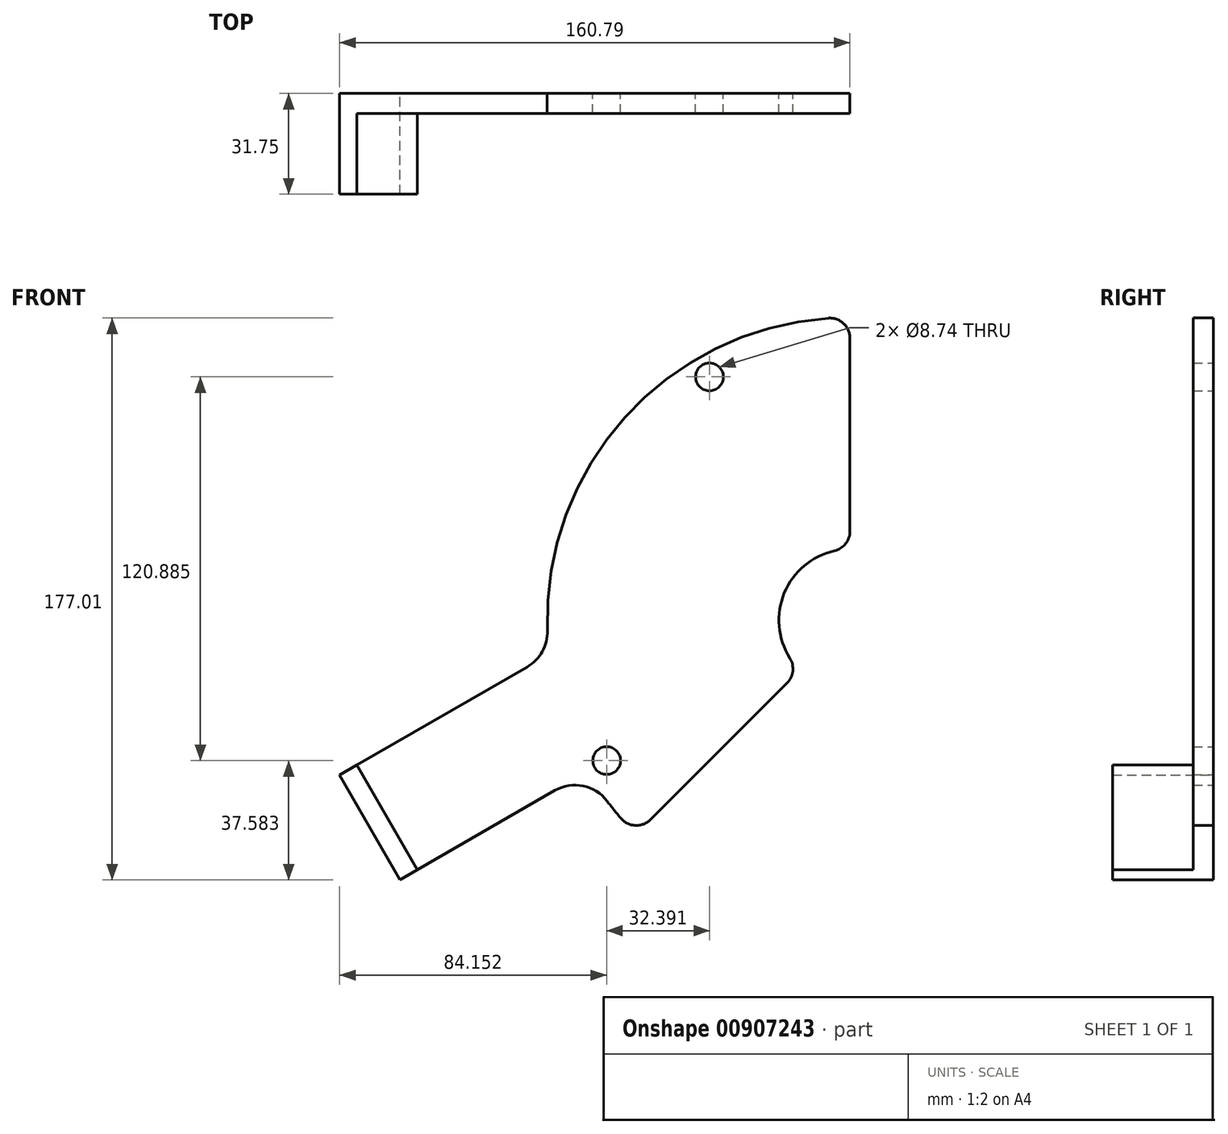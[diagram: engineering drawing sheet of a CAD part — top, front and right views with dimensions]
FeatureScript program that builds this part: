
annotation { "Feature Type Name" : "Feature", "Feature Type Description" : "" }
export const myFeature = defineFeature(function(context is Context, id is Id, definition is map)
    precondition{}
    {
        {
            var Q0;
            Q0=qCreatedBy(makeId("Front.planeOp"),FACE);
            var sketch = newSketch(context, id + "F0", { "sketchPlane" : qUnion([Q0])});
            skLineSegment(sketch, "E0", {"start": v(-82.62, -47.7) * mm, "end": v(-141.74, -81.83) * mm});
            skLineSegment(sketch, "E1", {"start": v(-141.74, -81.83) * mm, "end": v(-160.79, -48.84) * mm});
            skLineSegment(sketch, "E2", {"start": v(-160.79, -48.84) * mm, "end": v(-94.8, -10.74) * mm});
            skArc(sketch, "E3", {"start": v(0, 95.4) * mm, "mid": v(-71.15, 63.55) * mm, "end": v(-94.8, -10.74) * mm});
            skArc(sketch, "E4", {"start": v(0, 22.38) * mm, "mid": v(-20.67, 8.56) * mm, "end": v(-15.82, -15.82) * mm});
            skLineSegment(sketch, "E5", {"start": v(0, 0) * mm, "end": v(67.46, 67.46) * mm, "construction": true});
            skLineSegment(sketch, "E6", {"start": v(-15.82, -15.82) * mm, "end": v(-67.46, -67.46) * mm});
            skLineSegment(sketch, "E7", {"start": v(0, 0) * mm, "end": v(-82.62, -47.7) * mm, "construction": true});
            skArc(sketch, "E8.trimOffspring", {"start": v(-82.62, -47.7) * mm, "mid": v(-75.69, -58.08) * mm, "end": v(-67.46, -67.46) * mm});
            skLineSegment(sketch, "E9", {"start": v(0, 22.38) * mm, "end": v(0, 95.4) * mm});
            skSolve(sketch);
        }
        {
            var Q0;
            Q0=qSketchRegion(id+"F0",true);
            extrude(context, id + "F1", {"entities" : qUnion([Q0]), "depth" : 6.35 * mm, "offsetDistance" : 25.4 * mm});
        }
        {
            var Q0;
            Q0=makeQuery(id+"F1.opExtrude","CAP_FACE",FACE,{"disambiguationData":[OSD([sQuery(id+"F0.wireOp",EDGE,"E0"),sQuery(id+"F0.wireOp",EDGE,"E1"),sQuery(id+"F0.wireOp",EDGE,"E2"),sQuery(id+"F0.wireOp",EDGE,"E3"),sQuery(id+"F0.wireOp",EDGE,"E4"),sQuery(id+"F0.wireOp",EDGE,"E5"),sQuery(id+"F0.wireOp",EDGE,"E6"),sQuery(id+"F0.wireOp",EDGE,"E8.trimOffspring")])],"isStart":false});
            var sketch = newSketch(context, id + "F2", { "sketchPlane" : qUnion([Q0])});
            skLineSegment(sketch, "E10", {"start": v(0, 0) * mm, "end": v(82.62, 47.7) * mm, "construction": true});
            skLineSegment(sketch, "E11", {"start": v(0, 0) * mm, "end": v(-47.7, 82.62) * mm, "construction": true});
            skLineSegment(sketch, "E12", {"start": v(0, 0) * mm, "end": v(47.7, -82.62) * mm, "construction": true});
            skLineSegment(sketch, "E13", {"start": v(0, 0) * mm, "end": v(-82.62, -47.7) * mm, "construction": true});
            skCircle(sketch, "E14", {"center": v(-44.25, 76.64) * mm, "radius": 5.8 * mm, "construction": true});
            skCircle(sketch, "E15", {"center": v(-76.64, -44.25) * mm, "radius": 5.8 * mm, "construction": true});
            skLineSegment(sketch, "E16", {"start": v(-44.28, 76.7) * mm, "end": v(-76.7, -44.28) * mm, "construction": true});
            skLineSegment(sketch, "E17", {"start": v(-76.7, -44.28) * mm, "end": v(44.28, -76.7) * mm, "construction": true});
            skLineSegment(sketch, "E18", {"start": v(44.28, -76.7) * mm, "end": v(76.7, 44.28) * mm, "construction": true});
            skLineSegment(sketch, "E19", {"start": v(76.7, 44.28) * mm, "end": v(-44.28, 76.7) * mm, "construction": true});
            skSolve(sketch);
        }
        {
            var Q0;
            Q0=sQuery(id+"F2.wireOp",VERTEX,"E14.center");
            var Q1;
            Q1=sQuery(id+"F2.wireOp",VERTEX,"E15.center");
            var Q2;
            Q2=makeQuery(id+"F1.opExtrude","SWEPT_BODY",BODY,{"disambiguationData":[OSD([sQuery(id+"F0.wireOp",EDGE,"E0"),sQuery(id+"F0.wireOp",EDGE,"E1"),sQuery(id+"F0.wireOp",EDGE,"E2"),sQuery(id+"F0.wireOp",EDGE,"E3"),sQuery(id+"F0.wireOp",EDGE,"E4"),sQuery(id+"F0.wireOp",EDGE,"E5"),sQuery(id+"F0.wireOp",EDGE,"E6"),sQuery(id+"F0.wireOp",EDGE,"E8.trimOffspring")])]});
            hole(context, id + "F3", {"style" : HoleStyle.SIMPLE, "endStyle" : HoleEndStyle.THROUGH, "standardTappedOrClearance" : lookupTablePath({ "fit" : "Normal (ASME)", "standard" : "ANSI", "size" : "5/16", "type" : "Clearance" }), "standardBlindInLast" : lookupTablePath({ "fit" : "Normal", "standard" : "ANSI", "engagement" : "75%", "pitch" : "18 tpi", "size" : "5/16", "type" : "Clearance & tapped" }), "holeDiameter" : 8.74 * mm, "majorDiameter" : 6.35 * mm, "isTappedThrough" : true, "tappedDepth" : 8.47 * mm, "tapClearance" : 3, "locations" : qUnion([Q0, Q1]), "scope" : qUnion([Q2]), "startStyle" : HoleStartStyle.SKETCH});
        }
        {
            var Q0;
            Q0=makeQuery(id+"F1.opExtrude","CAP_FACE",FACE,{"disambiguationData":[OSD([sQuery(id+"F0.wireOp",EDGE,"E0"),sQuery(id+"F0.wireOp",EDGE,"E1"),sQuery(id+"F0.wireOp",EDGE,"E2"),sQuery(id+"F0.wireOp",EDGE,"E3"),sQuery(id+"F0.wireOp",EDGE,"E4"),sQuery(id+"F0.wireOp",EDGE,"E5"),sQuery(id+"F0.wireOp",EDGE,"E6"),sQuery(id+"F0.wireOp",EDGE,"E8.trimOffspring")])],"isStart":false});
            var sketch = newSketch(context, id + "F4", { "sketchPlane" : qUnion([Q0])});
            skLineSegment(sketch, "E20", {"start": v(-155.29, -45.66) * mm, "end": v(-136.24, -78.66) * mm});
            skLineSegment(sketch, "E21", {"start": v(-155.29, -45.66) * mm, "end": v(-160.79, -48.84) * mm});
            skLineSegment(sketch, "E22", {"start": v(-160.79, -48.84) * mm, "end": v(-141.74, -81.83) * mm});
            skLineSegment(sketch, "E23", {"start": v(-141.74, -81.83) * mm, "end": v(-136.24, -78.66) * mm});
            skSolve(sketch);
        }
        {
            var Q0;
            Q0 = qSketchRegion(id + "F4", true);
            extrude(context, id + "F5", {"entities" : qUnion([Q0]), "operationType" : NewBodyOperationType.ADD, "depth" : 25.4 * mm, "offsetDistance" : 25.4 * mm});
        }
        {
            var Q0;
            Q0=makeQuery(id+"F1.opExtrude","SWEPT_EDGE",EDGE,{"disambiguationData":[OSD([sQuery(id+"F0.wireOp",EDGE,"E0"),sQuery(id+"F0.wireOp",EDGE,"E8.trimOffspring")])]});
            var Q1;
            Q1=makeQuery(id+"F1.opExtrude","SWEPT_EDGE",EDGE,{"disambiguationData":[OSD([sQuery(id+"F0.wireOp",EDGE,"E2"),sQuery(id+"F0.wireOp",EDGE,"E3")])]});
            fillet(context, id + "F6", {"entities" : qUnion([Q0, Q1]), "radius" : 12.7 * mm, "tangentPropagation" : true, "allowEdgeOverflow" : false});
        }
        {
            var Q0;
            Q0=makeQuery(id+"F1.opExtrude","SWEPT_EDGE",EDGE,{"disambiguationData":[OSD([sQuery(id+"F0.wireOp",EDGE,"E6"),sQuery(id+"F0.wireOp",EDGE,"E8.trimOffspring")])]});
            var Q1;
            Q1=makeQuery(id+"F1.opExtrude","SWEPT_EDGE",EDGE,{"disambiguationData":[OSD([sQuery(id+"F0.wireOp",EDGE,"E4"),sQuery(id+"F0.wireOp",EDGE,"E6")])]});
            var Q2;
            Q2=makeQuery(id+"F1.opExtrude","SWEPT_EDGE",EDGE,{"disambiguationData":[OSD([sQuery(id+"F0.wireOp",EDGE,"E4"),sQuery(id+"F0.wireOp",EDGE,"E9")])]});
            var Q3;
            Q3=makeQuery(id+"F1.opExtrude","SWEPT_EDGE",EDGE,{"disambiguationData":[OSD([sQuery(id+"F0.wireOp",EDGE,"E3"),sQuery(id+"F0.wireOp",EDGE,"E9")])]});
            fillet(context, id + "F7", {"entities" : qUnion([Q0, Q1, Q2, Q3]), "radius" : 6.35 * mm, "tangentPropagation" : true, "allowEdgeOverflow" : false});
        }
    });
